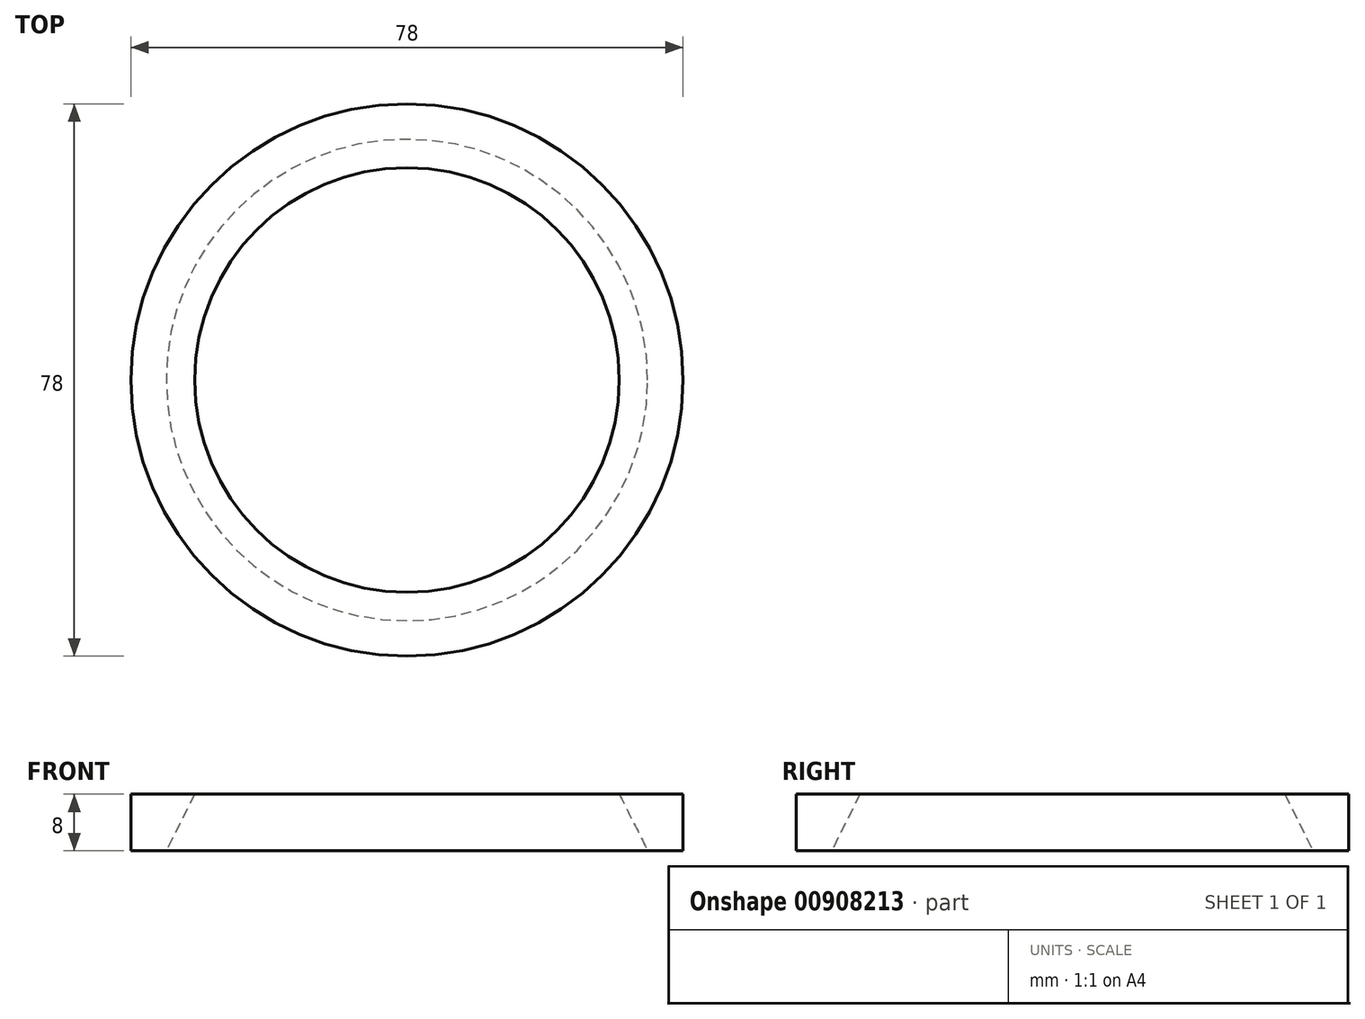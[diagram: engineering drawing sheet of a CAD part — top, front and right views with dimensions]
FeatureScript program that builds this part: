
annotation { "Feature Type Name" : "Feature", "Feature Type Description" : "" }
export const myFeature = defineFeature(function(context is Context, id is Id, definition is map)
    precondition{}
    {
        {
            var Q0;
            Q0=qCreatedBy(makeId("Top.planeOp"),FACE);
            var sketch = newSketch(context, id + "F0", { "sketchPlane" : qUnion([Q0])});
            skCircle(sketch, "E0", {"center": v(0, 0) * mm, "radius": 30 * mm});
            skCircle(sketch, "E1", {"center": v(0, 0) * mm, "radius": 39 * mm});
            skSolve(sketch);
        }
        {
            var Q0;
            Q0 = qSketchRegion(id + "F0", true);
            extrude(context, id + "F1", {"entities" : qUnion([Q0]), "depth" : 8 * mm, "offsetDistance" : 25 * mm});
        }
        {
            var Q0;
            Q0=qCreatedBy(makeId("Right.planeOp"),FACE);
            var sketch = newSketch(context, id + "F2", { "sketchPlane" : qUnion([Q0])});
            skLineSegment(sketch, "E2", {"start": v(-30, 0) * mm, "end": v(-30, 8) * mm});
            skLineSegment(sketch, "E3", {"start": v(-30, 0) * mm, "end": v(-34, 0) * mm});
            skLineSegment(sketch, "E4", {"start": v(-34, 0) * mm, "end": v(-30, 8) * mm});
            skSolve(sketch);
        }
        {
            var Q0;
            Q0 = qSketchRegion(id + "F2", true);
            var Q1;
            Q1=makeQuery(id+"F1.opExtrude","SWEPT_FACE",FACE,{"disambiguationData":[OSD([sQuery(id+"F0.wireOp",EDGE,"E0")])]});
            revolve(context, id + "F3", {"operationType" : NewBodyOperationType.REMOVE, "surfaceOperationType" : NewSurfaceOperationType.NEW, "entities" : qUnion([Q0]), "axis" : qUnion([Q1]), "revolveType" : RevolveType.FULL, "oppositeDirection" : true});
        }
    });
